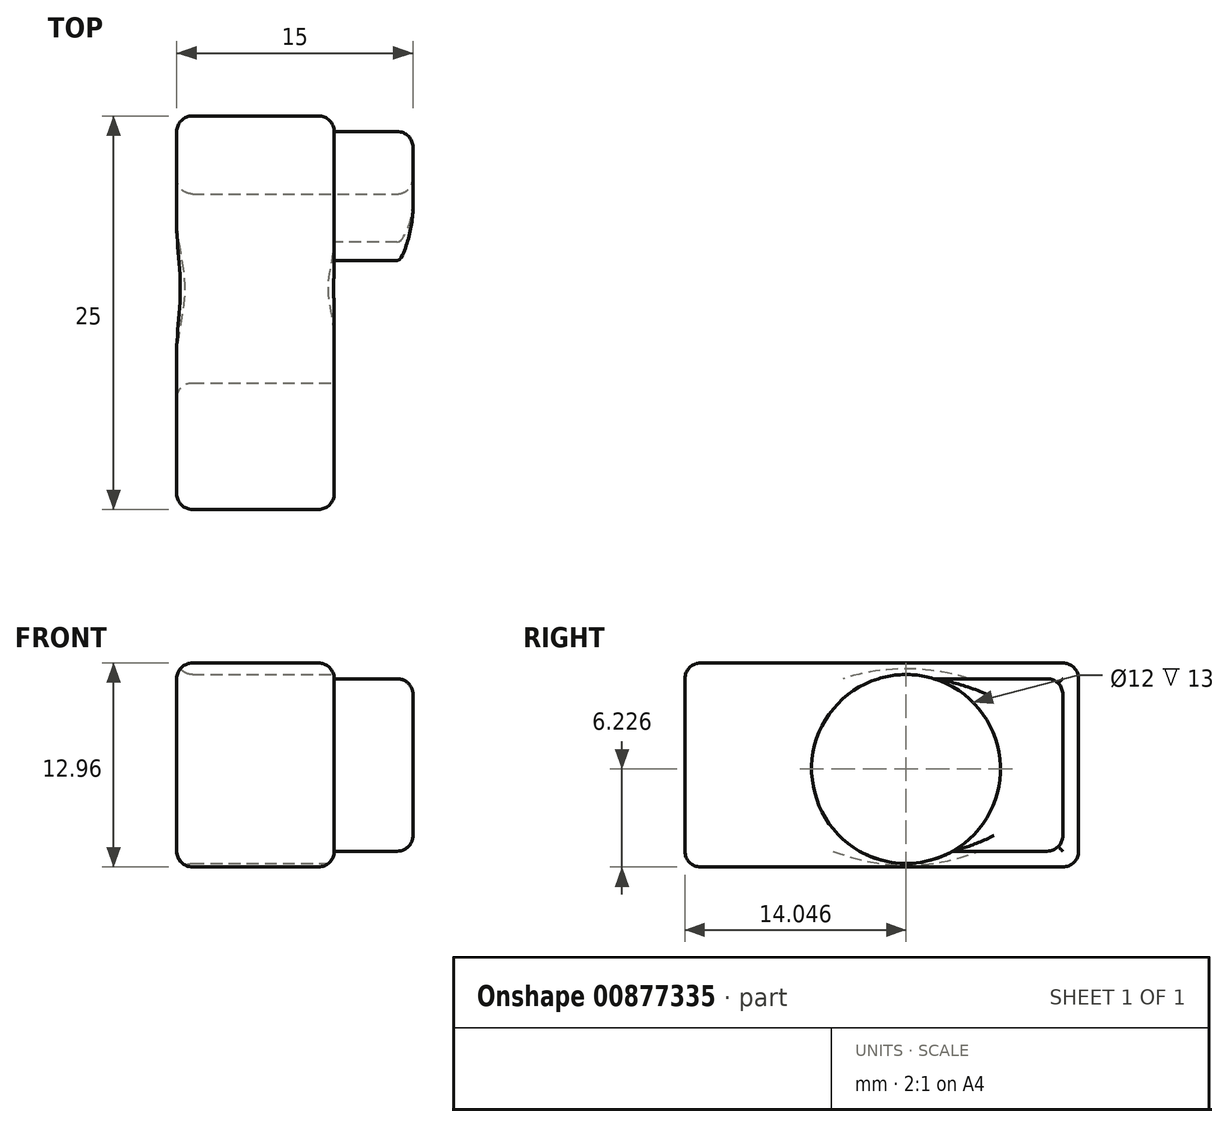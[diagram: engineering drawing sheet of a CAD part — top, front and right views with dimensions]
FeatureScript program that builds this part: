
annotation { "Feature Type Name" : "Feature", "Feature Type Description" : "" }
export const myFeature = defineFeature(function(context is Context, id is Id, definition is map)
    precondition{}
    {
        {
            var Q0;
            Q0=qCreatedBy(makeId("Top.planeOp"),FACE);
            var sketch = newSketch(context, id + "F0", { "sketchPlane" : qUnion([Q0])});
            skLineSegment(sketch, "E0.bottom", {"start": v(-5.42, 52.12) * mm, "end": v(-15.42, 52.12) * mm});
            skLineSegment(sketch, "E0.top", {"start": v(-5.42, 27.12) * mm, "end": v(-15.42, 27.12) * mm});
            skLineSegment(sketch, "E0.left", {"start": v(-5.42, 52.12) * mm, "end": v(-5.42, 27.12) * mm});
            skLineSegment(sketch, "E0.right", {"start": v(-15.42, 52.12) * mm, "end": v(-15.42, 27.12) * mm});
            skPoint(sketch, "E0.middle", {"position": v(-10.42, 39.62) * mm});
            skSolve(sketch);
        }
        {
            var Q0;
            Q0=makeQuery(id+"F0.imprint","IMPRINT",FACE,{"disambiguationData":[TD([[makeQuery(id+"F0.imprint","IMPRINT",EDGE,{"derivedFrom":sQuery(id+"F0.wireOp",EDGE,"E0.bottom")}),1.0]])]});
            extrude(context, id + "F1", {"entities" : qUnion([Q0]), "oppositeDirection" : true, "depth" : 12.96 * mm, "offsetDistance" : 25 * mm});
        }
        {
            var Q0;
            Q0=makeQuery(id+"F1.opExtrude","SWEPT_FACE",FACE,{"disambiguationData":[OSD([sQuery(id+"F0.wireOp",EDGE,"E0.left")])]});
            var sketch = newSketch(context, id + "F2", { "sketchPlane" : qUnion([Q0])});
            skSolve(sketch);
        }
        {
            var Q0;
            {var subQ0=sQuery(id+"F0.wireOp",EDGE,"E0.left");Q0=makeQuery(id+"F2.imprint","IMPRINT",FACE,{"disambiguationData":[TD([[makeQuery(id+"F2.imprint","IMPRINT",EDGE,{"derivedFrom":makeQuery(id+"F1.opExtrude","CAP_EDGE",EDGE,{"disambiguationData":[OSD([subQ0])],"isStart":true})}),1.0]])]});}
            var sketch = newSketch(context, id + "F3", { "sketchPlane" : qUnion([Q0])});
            skCircle(sketch, "E1", {"center": v(41.17, -6.73) * mm, "radius": 6 * mm});
            skSolve(sketch);
        }
        {
            var Q0;
            Q0=makeQuery(id+"F3.imprint","IMPRINT",FACE,{"disambiguationData":[TD([[makeQuery(id+"F3.imprint","IMPRINT",EDGE,{"derivedFrom":sQuery(id+"F3.wireOp",EDGE,"E1")}),1.0]])]});
            var Q1;
            Q1 = qSketchRegion(id + "F3", true);
            extrude(context, id + "F4", {"entities" : qUnion([Q0, Q1]), "operationType" : NewBodyOperationType.REMOVE, "oppositeDirection" : true, "depth" : 24.66 * mm, "offsetDistance" : 25 * mm});
        }
        {
            var Q0;
            Q0=makeQuery(id+"F4.boolean.opBoolean","INTERSECT",EDGE,{"derivedFrom":[makeQuery(id+"F1.opExtrude","SWEPT_FACE",FACE,{"disambiguationData":[OSD([sQuery(id+"F0.wireOp",EDGE,"E0.right")])]}),makeQuery(id+"F4.opExtrude","SWEPT_FACE",FACE,{"disambiguationData":[OSD([sQuery(id+"F3.wireOp",EDGE,"E1")])]})]});
            var Q1;
            Q1=makeQuery(id+"F1.opExtrude","SWEPT_FACE",FACE,{"disambiguationData":[OSD([sQuery(id+"F0.wireOp",EDGE,"E0.bottom")])]});
            var Q2;
            Q2=makeQuery(id+"F1.opExtrude","CAP_EDGE",EDGE,{"disambiguationData":[OSD([sQuery(id+"F0.wireOp",EDGE,"E0.top")])],"isStart":true});
            var Q3;
            Q3=makeQuery(id+"F1.opExtrude","CAP_EDGE",EDGE,{"disambiguationData":[OSD([sQuery(id+"F0.wireOp",EDGE,"E0.right")])],"isStart":true});
            var Q4;
            Q4=makeQuery(id+"F1.opExtrude","CAP_EDGE",EDGE,{"disambiguationData":[OSD([sQuery(id+"F0.wireOp",EDGE,"E0.left")])],"isStart":true});
            var Q5;
            Q5=makeQuery(id+"F1.opExtrude","CAP_EDGE",EDGE,{"disambiguationData":[OSD([sQuery(id+"F0.wireOp",EDGE,"E0.right")])],"isStart":false});
            var Q6;
            Q6=makeQuery(id+"F1.opExtrude","CAP_EDGE",EDGE,{"disambiguationData":[OSD([sQuery(id+"F0.wireOp",EDGE,"E0.top")])],"isStart":false});
            var Q7;
            Q7=makeQuery(id+"F1.opExtrude","SWEPT_EDGE",EDGE,{"disambiguationData":[OSD([sQuery(id+"F0.wireOp",EDGE,"E0.top"),sQuery(id+"F0.wireOp",EDGE,"E0.right")])]});
            var Q8;
            Q8=makeQuery(id+"F1.opExtrude","SWEPT_EDGE",EDGE,{"disambiguationData":[OSD([sQuery(id+"F0.wireOp",EDGE,"E0.top"),sQuery(id+"F0.wireOp",EDGE,"E0.left")])]});
            var Q9;
            Q9=makeQuery(id+"F1.opExtrude","CAP_EDGE",EDGE,{"disambiguationData":[OSD([sQuery(id+"F0.wireOp",EDGE,"E0.left")])],"isStart":false});
            fillet(context, id + "F5", {"entities" : qUnion([Q0, Q1, Q2, Q3, Q4, Q5, Q6, Q7, Q8, Q9]), "radius" : 1 * mm, "tangentPropagation" : true, "allowEdgeOverflow" : false});
        }
        {
            var Q0;
            Q0=makeQuery(id+"F5.opFillet","SPLIT",FACE,{"disambiguationData":[OD(0.0)],"derivedFrom":makeQuery(id+"F1.opExtrude","SWEPT_FACE",FACE,{"disambiguationData":[OSD([sQuery(id+"F0.wireOp",EDGE,"E0.left")])]})});
            extrude(context, id + "F6", {"entities" : qUnion([Q0]), "operationType" : NewBodyOperationType.ADD, "depth" : 5 * mm, "offsetDistance" : 25 * mm});
        }
        {
            var Q0;
            {var subQ0=sQuery(id+"F0.wireOp",EDGE,"E0.left");Q0=makeQuery(id+"F6.opExtrude","CAP_EDGE",EDGE,{"disambiguationData":[OSD([subQ0]),TDD([makeQuery(id+"F5.opFillet","BLEND_EDGE",EDGE,{"disambiguationData":[OD(0.0)],"blendedFrom":[makeQuery(id+"F1.opExtrude","CAP_EDGE",EDGE,{"disambiguationData":[OSD([subQ0])],"isStart":false}),makeQuery(id+"F1.opExtrude","SWEPT_FACE",FACE,{"disambiguationData":[OSD([subQ0])]})],"blendedInto":[makeQuery(id+"F1.opExtrude","SWEPT_FACE",FACE,{"disambiguationData":[OSD([subQ0])]})]})])],"isStart":false});}
            var Q1;
            {var subQ0=sQuery(id+"F0.wireOp",EDGE,"E0.left");Q1=makeQuery(id+"F6.opExtrude","CAP_EDGE",EDGE,{"disambiguationData":[OSD([subQ0]),TDD([makeQuery(id+"F5.opFillet","BLEND_EDGE",EDGE,{"disambiguationData":[OD(0.0)],"blendedFrom":[makeQuery(id+"F1.opExtrude","CAP_EDGE",EDGE,{"disambiguationData":[OSD([subQ0])],"isStart":true}),makeQuery(id+"F1.opExtrude","SWEPT_FACE",FACE,{"disambiguationData":[OSD([subQ0])]})],"blendedInto":[makeQuery(id+"F1.opExtrude","SWEPT_FACE",FACE,{"disambiguationData":[OSD([subQ0])]})]})])],"isStart":false});}
            var Q2;
            {var subQ0=sQuery(id+"F0.wireOp",EDGE,"E0.left");var subQ1=sQuery(id+"F0.wireOp",EDGE,"E0.bottom");Q2=makeQuery(id+"F6.opExtrude","SWEPT_EDGE",EDGE,{"disambiguationData":[OSD([subQ1,subQ0]),TDD([makeQuery(id+"F5.opFillet","BLEND_VERTEX",VERTEX,{"blendedFrom":[makeQuery(id+"F1.opExtrude","CAP_VERTEX",VERTEX,{"disambiguationData":[OSD([subQ1,subQ0])],"isStart":false}),makeQuery(id+"F1.opExtrude","SWEPT_EDGE",EDGE,{"disambiguationData":[OSD([subQ1,subQ0])]}),makeQuery(id+"F1.opExtrude","CAP_EDGE",EDGE,{"disambiguationData":[OSD([subQ0])],"isStart":false}),makeQuery(id+"F1.opExtrude","SWEPT_FACE",FACE,{"disambiguationData":[OSD([subQ0])]})],"blendedInto":[makeQuery(id+"F1.opExtrude","SWEPT_FACE",FACE,{"disambiguationData":[OSD([subQ0])]})]})])]});}
            var Q3;
            Q3=makeQuery(id+"F6.opExtrude","CAP_EDGE",EDGE,{"disambiguationData":[OSD([sQuery(id+"F0.wireOp",EDGE,"E0.bottom"),sQuery(id+"F0.wireOp",EDGE,"E0.left")])],"isStart":false});
            var Q4;
            {var subQ0=sQuery(id+"F0.wireOp",EDGE,"E0.left");var subQ1=sQuery(id+"F0.wireOp",EDGE,"E0.bottom");Q4=makeQuery(id+"F6.opExtrude","SWEPT_EDGE",EDGE,{"disambiguationData":[OSD([subQ1,subQ0]),TDD([makeQuery(id+"F5.opFillet","BLEND_VERTEX",VERTEX,{"blendedFrom":[makeQuery(id+"F1.opExtrude","CAP_VERTEX",VERTEX,{"disambiguationData":[OSD([subQ1,subQ0])],"isStart":true}),makeQuery(id+"F1.opExtrude","SWEPT_EDGE",EDGE,{"disambiguationData":[OSD([subQ1,subQ0])]}),makeQuery(id+"F1.opExtrude","CAP_EDGE",EDGE,{"disambiguationData":[OSD([subQ0])],"isStart":true}),makeQuery(id+"F1.opExtrude","SWEPT_FACE",FACE,{"disambiguationData":[OSD([subQ0])]})],"blendedInto":[makeQuery(id+"F1.opExtrude","SWEPT_FACE",FACE,{"disambiguationData":[OSD([subQ0])]})]})])]});}
            var Q5;
            Q5=makeQuery(id+"F6.opExtrude","CAP_EDGE",EDGE,{"disambiguationData":[OSD([sQuery(id+"F3.wireOp",EDGE,"E1")])],"isStart":false});
            fillet(context, id + "F7", {"entities" : qUnion([Q0, Q1, Q2, Q3, Q4, Q5]), "radius" : 1 * mm, "tangentPropagation" : true, "allowEdgeOverflow" : false});
        }
    });
